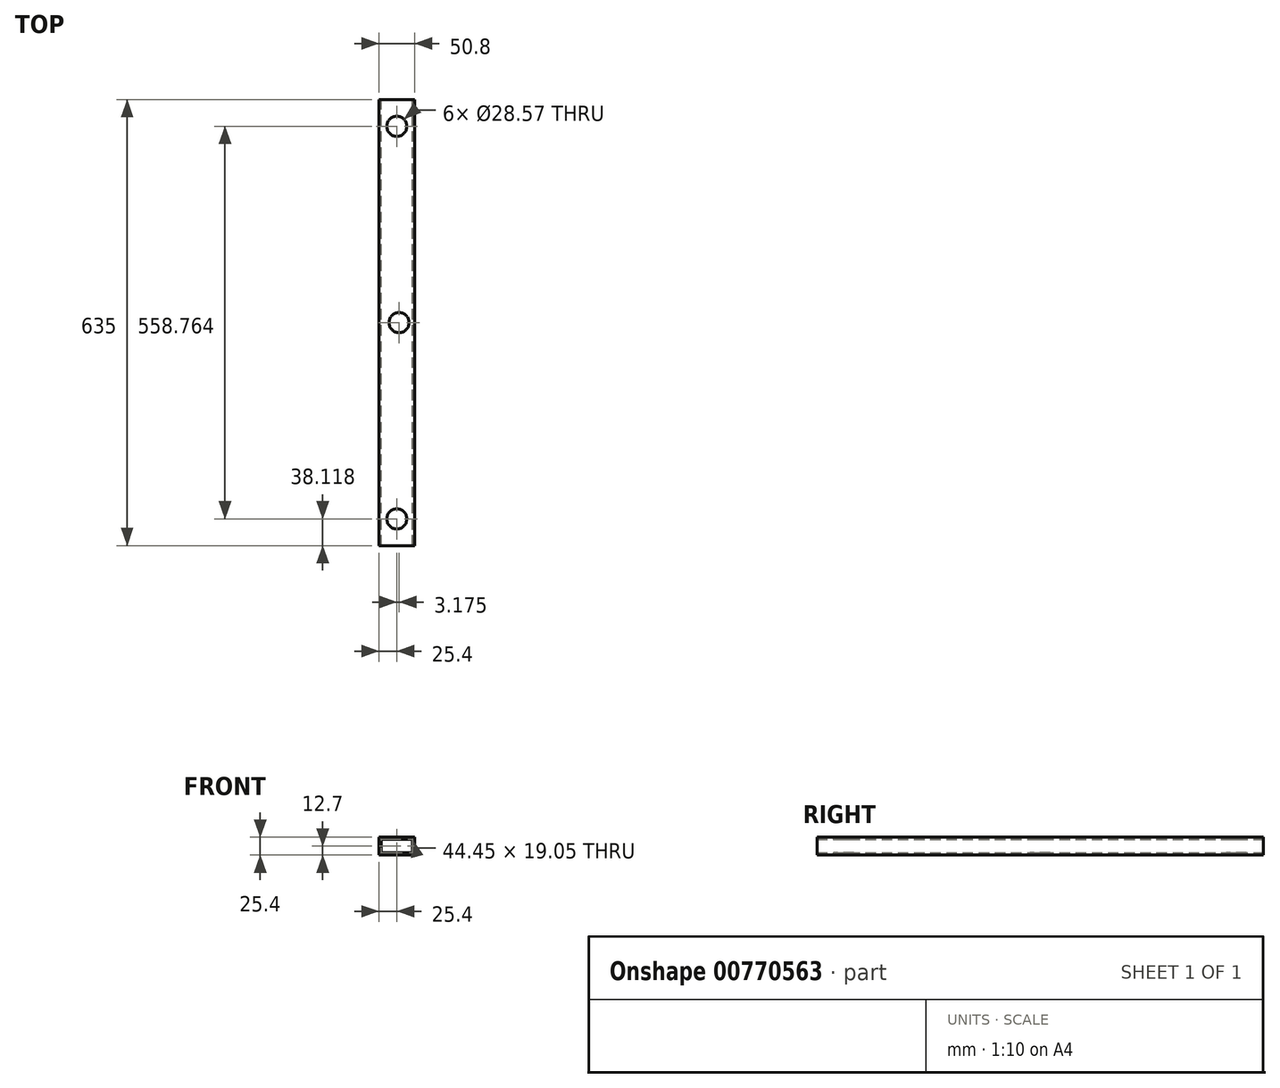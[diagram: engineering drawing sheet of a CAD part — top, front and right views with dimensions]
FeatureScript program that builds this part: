
annotation { "Feature Type Name" : "Feature", "Feature Type Description" : "" }
export const myFeature = defineFeature(function(context is Context, id is Id, definition is map)
    precondition{}
    {
        {
            var Q0;
            Q0=qCreatedBy(makeId("Front.planeOp"),FACE);
            var sketch = newSketch(context, id + "F0", { "sketchPlane" : qUnion([Q0])});
            skLineSegment(sketch, "E0", {"start": v(0, 0) * mm, "end": v(0, 25.4) * mm});
            skLineSegment(sketch, "E1", {"start": v(0, 25.4) * mm, "end": v(50.8, 25.4) * mm});
            skLineSegment(sketch, "E2", {"start": v(50.8, 25.4) * mm, "end": v(50.8, 0) * mm});
            skLineSegment(sketch, "E3", {"start": v(50.8, 0) * mm, "end": v(0, 0) * mm});
            skLineSegment(sketch, "E4.bottom", {"start": v(3.17, 22.23) * mm, "end": v(47.63, 22.23) * mm});
            skLineSegment(sketch, "E4.top", {"start": v(3.17, 3.17) * mm, "end": v(47.63, 3.17) * mm});
            skLineSegment(sketch, "E4.left", {"start": v(3.18, 22.23) * mm, "end": v(3.18, 3.17) * mm});
            skLineSegment(sketch, "E4.right", {"start": v(47.63, 22.23) * mm, "end": v(47.63, 3.17) * mm});
            skLineSegment(sketch, "E5", {"start": v(25.4, 25.4) * mm, "end": v(25.4, 22.23) * mm, "construction": true});
            skLineSegment(sketch, "E6", {"start": v(0, 12.7) * mm, "end": v(3.18, 12.7) * mm, "construction": true});
            skSolve(sketch);
        }
        {
            var Q0;
            Q0 = qSketchRegion(id + "F0", true);
            extrude(context, id + "F1", {"entities" : qUnion([Q0]), "depth" : 635 * mm, "offsetDistance" : 25.4 * mm});
        }
        {
            var Q0;
            Q0=makeQuery(id+"F1.opExtrude","SWEPT_FACE",FACE,{"disambiguationData":[OSD([sQuery(id+"F0.wireOp",EDGE,"E1")])]});
            var sketch = newSketch(context, id + "F2", { "sketchPlane" : qUnion([Q0])});
            skLineSegment(sketch, "E7", {"start": v(25.4, -38.12) * mm, "end": v(28.58, -317.5) * mm, "construction": true});
            skLineSegment(sketch, "E8", {"start": v(28.58, -317.5) * mm, "end": v(25.4, -596.88) * mm, "construction": true});
            skLineSegment(sketch, "E9", {"start": v(25.4, -596.88) * mm, "end": v(25.4, -38.12) * mm, "construction": true});
            skLineSegment(sketch, "E10", {"start": v(0, -317.5) * mm, "end": v(25.4, -317.5) * mm, "construction": true});
            skCircle(sketch, "E11", {"center": v(25.4, -38.12) * mm, "radius": 14.29 * mm});
            skCircle(sketch, "E12", {"center": v(28.58, -317.5) * mm, "radius": 14.29 * mm});
            skCircle(sketch, "E13", {"center": v(25.4, -596.88) * mm, "radius": 14.29 * mm});
            skSolve(sketch);
        }
        {
            var Q0;
            Q0 = qSketchRegion(id + "F2", true);
            extrude(context, id + "F3", {"entities" : qUnion([Q0]), "operationType" : NewBodyOperationType.REMOVE, "endBound" : BoundingType.THROUGH_ALL, "oppositeDirection" : true, "depth" : 25.4 * mm, "offsetDistance" : 25.4 * mm});
        }
    });
